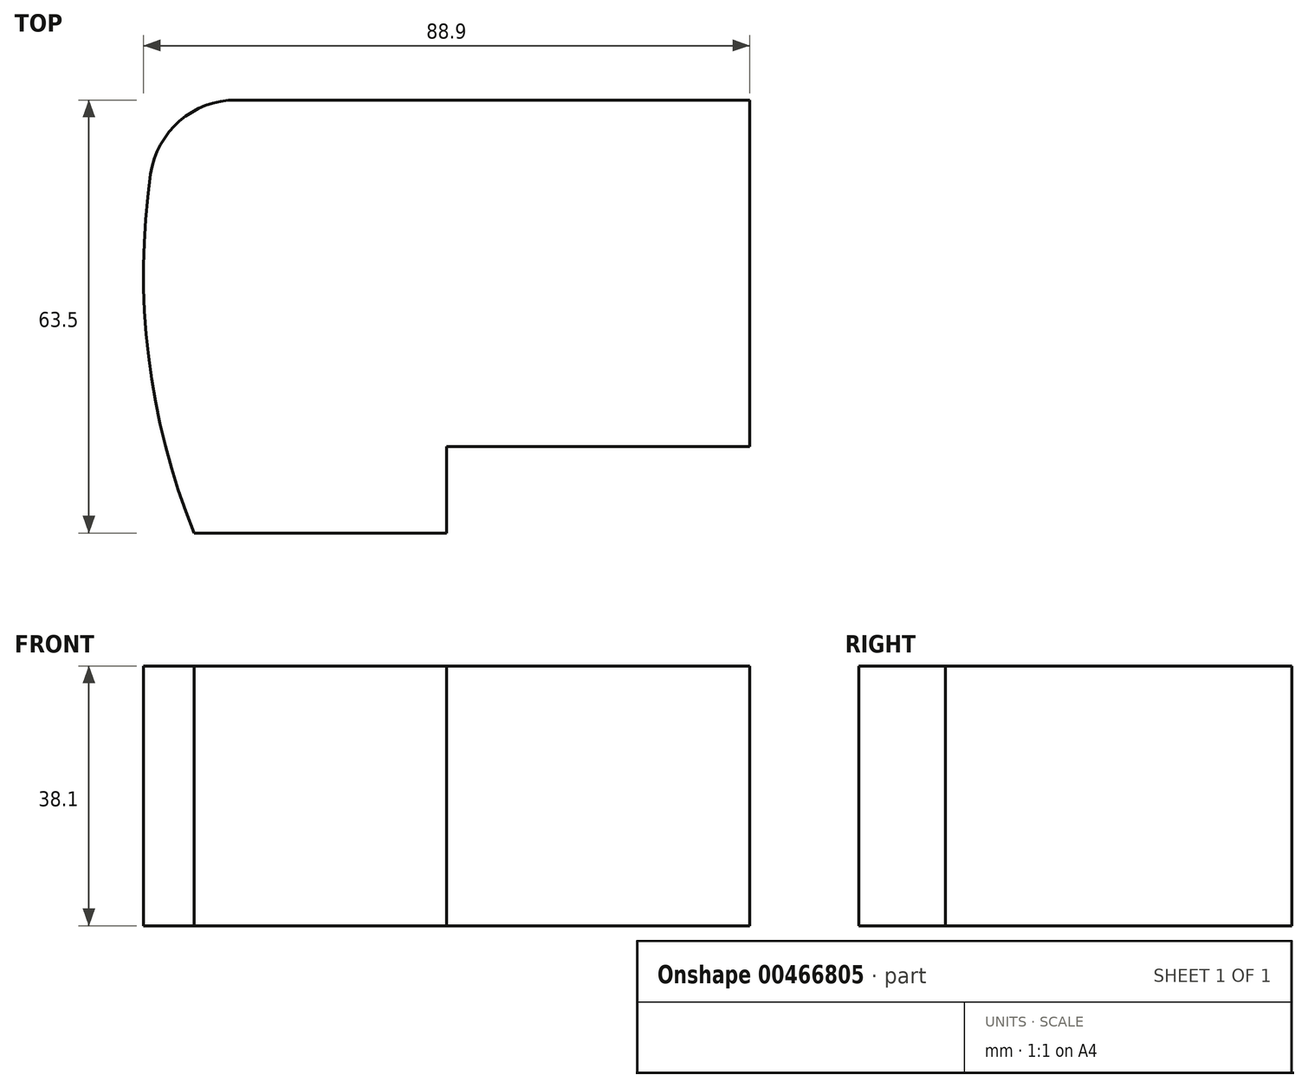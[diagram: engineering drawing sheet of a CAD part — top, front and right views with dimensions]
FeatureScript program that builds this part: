
annotation { "Feature Type Name" : "Feature", "Feature Type Description" : "" }
export const myFeature = defineFeature(function(context is Context, id is Id, definition is map)
    precondition{}
    {
        {
            var Q0;
            Q0=qCreatedBy(makeId("Top.planeOp"),FACE);
            var sketch = newSketch(context, id + "F0", { "sketchPlane" : qUnion([Q0])});
            skLineSegment(sketch, "E0.bottom", {"start": v(7.41, 0) * mm, "end": v(44.45, 0) * mm});
            skLineSegment(sketch, "E0.top", {"start": v(3.23, 63.5) * mm, "end": v(88.9, 63.5) * mm});
            skLineSegment(sketch, "E1.top", {"start": v(88.9, 12.7) * mm, "end": v(44.45, 12.7) * mm});
            skLineSegment(sketch, "E1.right", {"start": v(44.45, 0) * mm, "end": v(44.45, 0) * mm});
            skArc(sketch, "E2", {"start": v(3.23, 63.5) * mm, "mid": v(0.22, 31.41) * mm, "end": v(7.41, 0) * mm});
            skPoint(sketch, "E3.orphan", {"position": v(0, 0) * mm});
            skLineSegment(sketch, "E4", {"start": v(44.45, 0) * mm, "end": v(44.45, 12.7) * mm});
            skLineSegment(sketch, "E5", {"start": v(88.9, 12.7) * mm, "end": v(88.9, 63.5) * mm});
            skSolve(sketch);
        }
        {
            var Q0;
            Q0=makeQuery(id+"F0.imprint","IMPRINT",FACE,{"disambiguationData":[TD([[makeQuery(id+"F0.imprint","IMPRINT",EDGE,{"derivedFrom":sQuery(id+"F0.wireOp",EDGE,"E0.bottom")}),1.0]])]});
            extrude(context, id + "F1", {"entities" : qUnion([Q0]), "depth" : 38.1 * mm});
        }
        {
            var Q0;
            Q0=makeQuery(id+"F1.opExtrude","SWEPT_EDGE",EDGE,{"disambiguationData":[OSD([sQuery(id+"F0.wireOp",EDGE,"E0.top"),sQuery(id+"F0.wireOp",EDGE,"E2")])]});
            fillet(context, id + "F2", {"entities" : qUnion([Q0]), "radius" : 12.7 * mm, "tangentPropagation" : true, "allowEdgeOverflow" : false});
        }
    });
